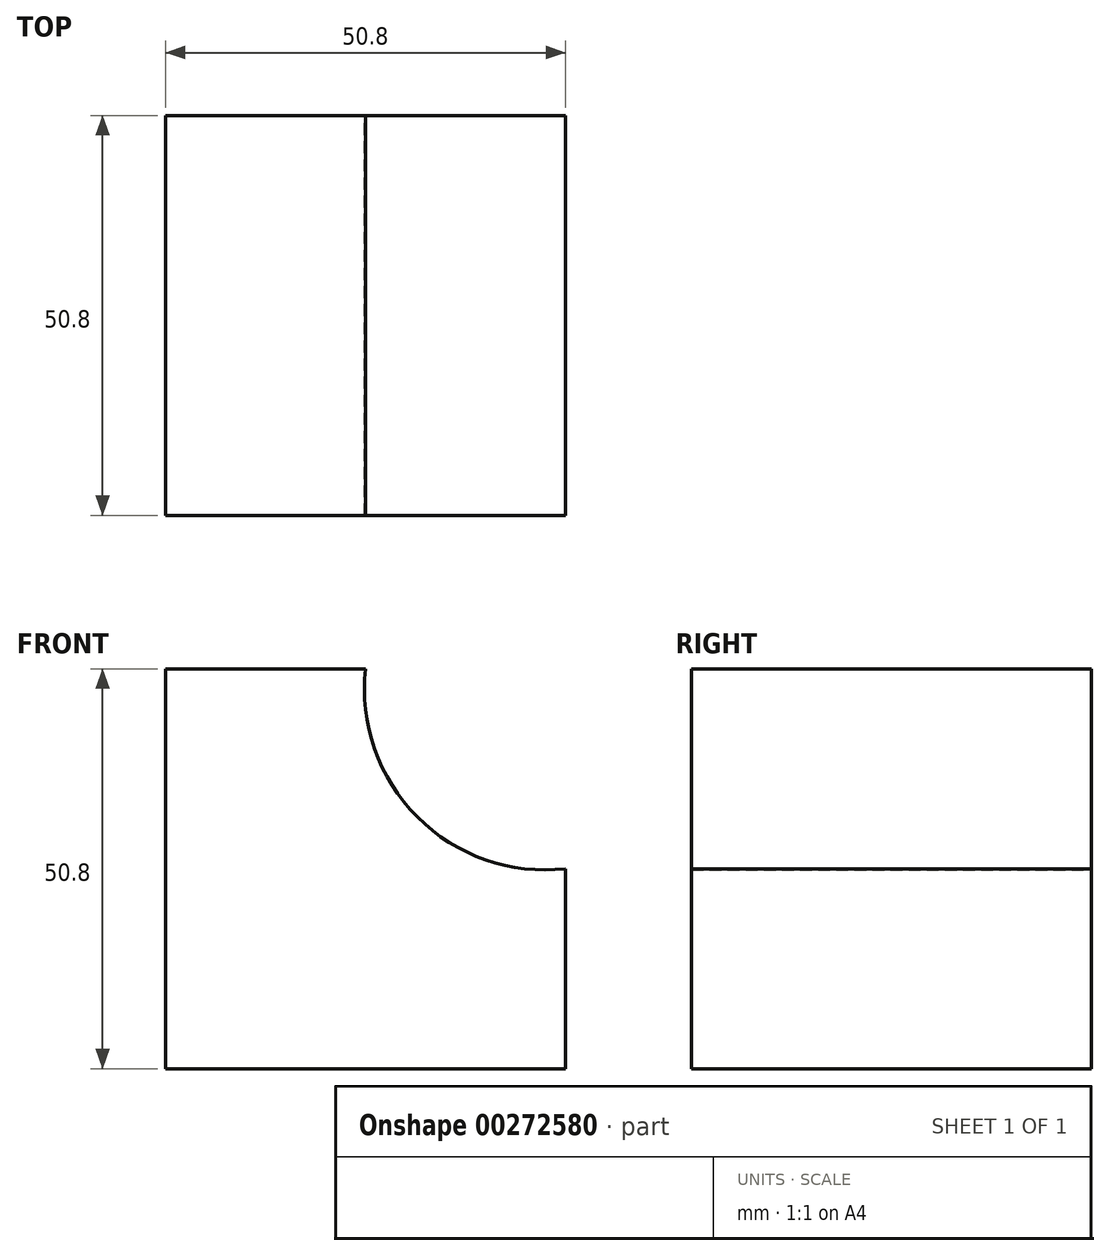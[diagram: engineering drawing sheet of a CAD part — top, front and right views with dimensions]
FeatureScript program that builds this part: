
annotation { "Feature Type Name" : "Feature", "Feature Type Description" : "" }
export const myFeature = defineFeature(function(context is Context, id is Id, definition is map)
    precondition{}
    {
        {
            var Q0;
            Q0=qCreatedBy(makeId("Front.planeOp"),FACE);
            var sketch = newSketch(context, id + "F0", { "sketchPlane" : qUnion([Q0])});
            skLineSegment(sketch, "E0", {"start": v(-61.3, 8.78) * mm, "end": v(-61.3, 59.58) * mm});
            skLineSegment(sketch, "E1", {"start": v(-61.3, 59.58) * mm, "end": v(-35.9, 59.58) * mm});
            skLineSegment(sketch, "E2", {"start": v(-10.5, 34.18) * mm, "end": v(-10.5, 8.78) * mm});
            skLineSegment(sketch, "E3", {"start": v(-10.5, 8.78) * mm, "end": v(-61.3, 8.78) * mm});
            skArc(sketch, "E4", {"start": v(-35.9, 59.58) * mm, "mid": v(-29.33, 40.75) * mm, "end": v(-10.5, 34.18) * mm});
            skSolve(sketch);
        }
        {
            var Q0;
            Q0=makeQuery(id+"F0.imprint","IMPRINT",FACE,{"disambiguationData":[TD([[makeQuery(id+"F0.imprint","IMPRINT",EDGE,{"derivedFrom":sQuery(id+"F0.wireOp",EDGE,"E0")}),-1.0]])]});
            extrude(context, id + "F1", {"entities" : qUnion([Q0]), "depth" : 50.8 * mm});
        }
    });
